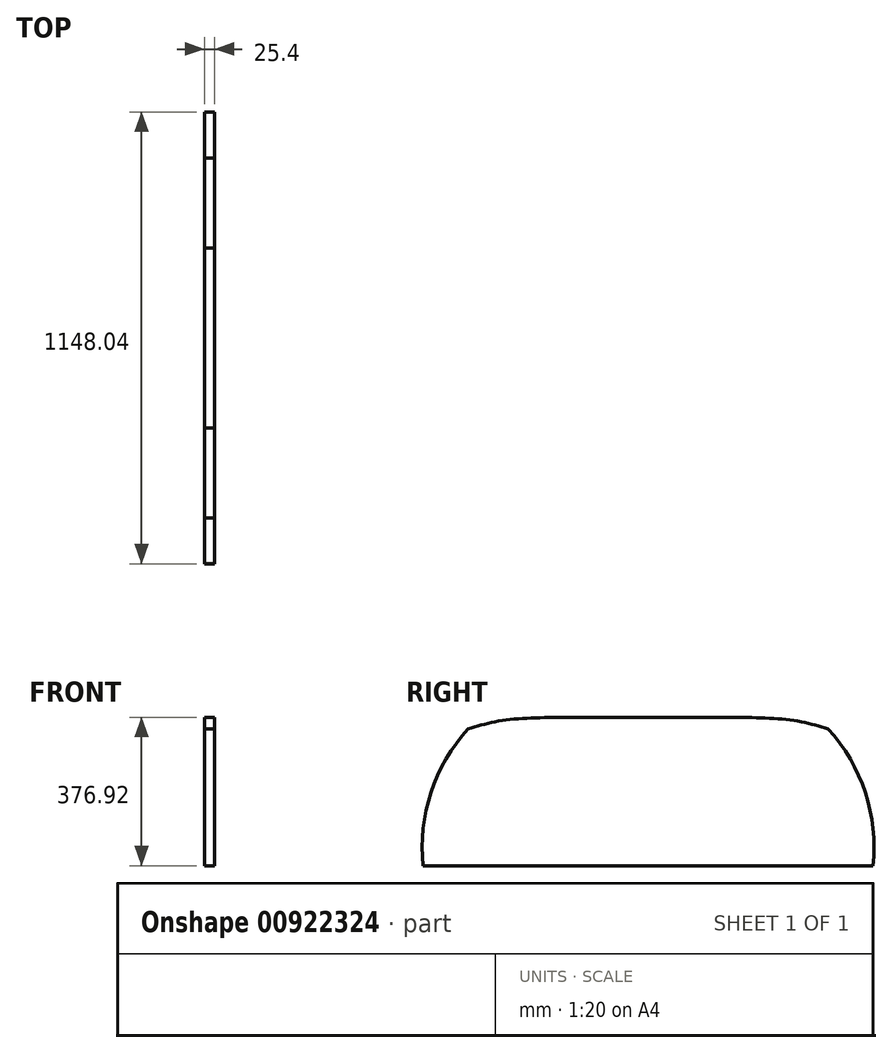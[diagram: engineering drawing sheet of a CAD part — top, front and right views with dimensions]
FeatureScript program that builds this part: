
annotation { "Feature Type Name" : "Feature", "Feature Type Description" : "" }
export const myFeature = defineFeature(function(context is Context, id is Id, definition is map)
    precondition{}
    {
        {
            var Q0;
            Q0=qCreatedBy(makeId("Right.planeOp"),FACE);
            var sketch = newSketch(context, id + "F0", { "sketchPlane" : qUnion([Q0])});
            skLineSegment(sketch, "E0", {"start": v(0, 376.92) * mm, "end": v(-228.6, 376.92) * mm});
            skFitSpline(sketch, "E1", {"points": [v(-457.28, 347.45) * mm, v(-367.01, 369.16) * mm, v(-228.6, 376.92) * mm], "startDerivative": vector(189.06, 55.92) * mm, "endDerivative": vector(265.74, 4.72) * mm});
            skArc(sketch, "E2", {"start": v(-457.28, 347.45) * mm, "mid": v(-551.69, 185.99) * mm, "end": v(-571.58, 0) * mm});
            skLineSegment(sketch, "E3", {"start": v(-571.58, 0) * mm, "end": v(0, 0) * mm});
            skLineSegment(sketch, "E4.MirrorCS", {"start": v(0, 376.92) * mm, "end": v(228.6, 376.92) * mm});
            skLineSegment(sketch, "E5.MirrorCS", {"start": v(571.58, 0) * mm, "end": v(0, 0) * mm});
            skArc(sketch, "E6.MirrorCS", {"start": v(457.28, 347.45) * mm, "mid": v(551.69, 185.99) * mm, "end": v(571.58, 0) * mm});
            skFitSpline(sketch, "E7.MirrorCS", {"points": [v(457.28, 347.45) * mm, v(367.01, 369.16) * mm, v(228.6, 376.92) * mm], "startDerivative": vector(-189.06, 55.92) * mm, "endDerivative": vector(-265.74, 4.72) * mm});
            skSolve(sketch);
        }
        {
            var Q0;
            Q0 = qSketchRegion(id + "F0", true);
            extrude(context, id + "F1", {"entities" : qUnion([Q0]), "depth" : 25.4 * mm, "offsetDistance" : 25.4 * mm});
        }
    });
